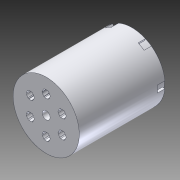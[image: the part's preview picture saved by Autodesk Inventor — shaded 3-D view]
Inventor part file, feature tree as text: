
AUTODESK INVENTOR PART (.ipt)
format: ipt  version: 2012 (Build 160160000, 160)  size: 552,448 bytes
history: native  units: mm
features: extrude x5, sketch x5, pattern_circular x2, other x1, helix x1, mirror x1
ambient origin geometry x8: Origin, YZ Plane, XZ Plane, XY Plane, X Axis, Y Axis, Z Axis, Center Point
bodies: Solid1 (feature_tree)
feature tree (15):
  extrude  "Extrusion1"  Depth=54.0mm
  extrude  "Extrusion2"  Depth=6.2mm
  sketch  "Sketch4"  dims[d15=100.0mm d16=0.0mm d17=15.0mm]
  other  "Work Axis1"
  helix  "Coil1"  [1 undecoded]
  pattern_circular  "Circular Pattern1"  Count=6 Angle=360.0deg
  sketch  "Sketch12"  dims[d18=1.0mm d19=2.9mm]
  extrude  "Extrusion10"  Depth=15.0mm
  extrude  "Extrusion11"  Depth=2.9mm
  extrude  "Extrusion12"  Depth=5.588mm
  mirror  "Mirror2"
  pattern_circular  "Circular Pattern4"  Count=10 Angle=360.0deg
  sketch  "Sketch2"  dims[d0=6.4mm d4=54.0mm]
  sketch  "Sketch3"  dims[d5=34.0mm d6=36.0mm d7=0.0mm d8=0.0mm d9=6.2mm d10=15.0mm d11=60.0mm d13=360.0deg]
  sketch  "Sketch14"  dims[d20=60.0mm d22=360.0deg d24=5.588mm d25=406.4mm d26=10.0mm d27=10.0mm d28=0.0mm d29=90.0deg d30=90.0deg d31=0.0mm d32=0.0mm d33=100.0mm d34=0.0mm d35=60.0mm d36=360.0deg d82=7.5mm d83=60.0mm d85=360.0deg d87=50.0mm d88=32.0mm d89=35.25mm d90=1.5mm d91=0.0mm d92=14.25mm d93=0.0mm d94=0.0mm d96=1.047198mm d103=30.0deg d104=1.047198mm d105=50.0mm d106=1.047198mm d107=6.0mm d108=0.0mm d109=60.0mm d110=360.0deg]
note: 1 required parameter value undecoded (feature->parameter linkage not recoverable at this tier; creation-order binding heuristic only, values carry confidence <= 0.55)
